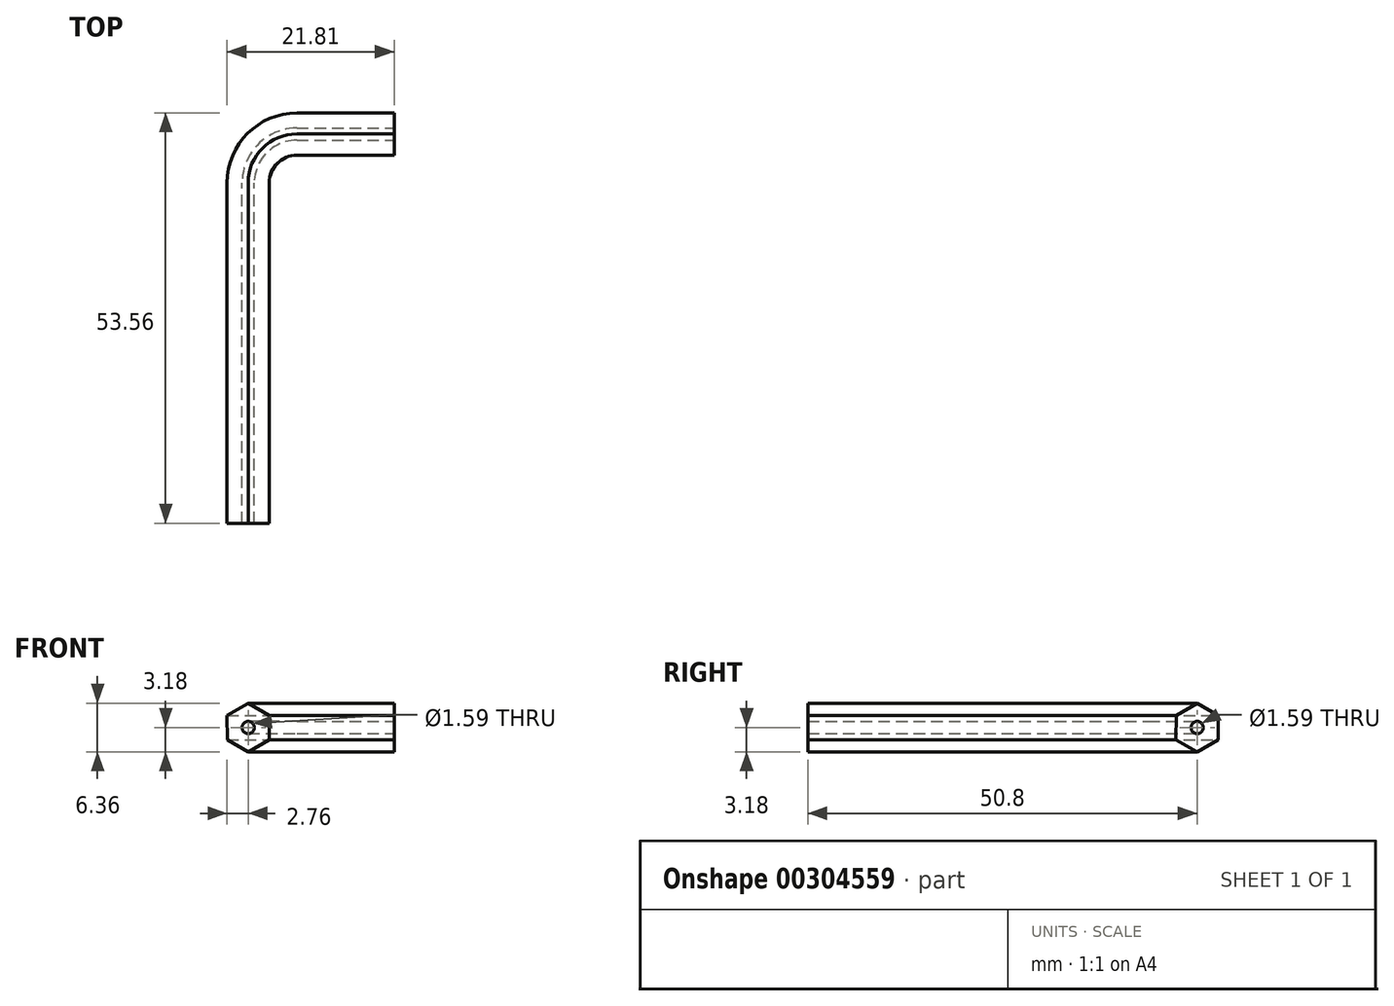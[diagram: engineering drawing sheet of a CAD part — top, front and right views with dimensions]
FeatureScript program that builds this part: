
annotation { "Feature Type Name" : "Feature", "Feature Type Description" : "" }
export const myFeature = defineFeature(function(context is Context, id is Id, definition is map)
    precondition{}
    {
        {
            var Q0;
            Q0=qCreatedBy(makeId("Front.planeOp"),FACE);
            var sketch = newSketch(context, id + "F0", { "sketchPlane" : qUnion([Q0])});
            skCircle(sketch, "E0.cCircle", {"center": v(0, 0) * mm, "radius": 3.18 * mm, "construction": true});
            skLineSegment(sketch, "E0.0", {"start": v(2.76, -1.58) * mm, "end": v(0.01, -3.17) * mm});
            skLineSegment(sketch, "E0.1", {"start": v(0.01, -3.18) * mm, "end": v(-2.74, -1.6) * mm});
            skLineSegment(sketch, "E0.2", {"start": v(-2.74, -1.6) * mm, "end": v(-2.76, 1.58) * mm});
            skLineSegment(sketch, "E0.3", {"start": v(-2.76, 1.58) * mm, "end": v(-0.01, 3.18) * mm});
            skLineSegment(sketch, "E0.4", {"start": v(-0.01, 3.18) * mm, "end": v(2.74, 1.6) * mm});
            skLineSegment(sketch, "E0.5", {"start": v(2.74, 1.6) * mm, "end": v(2.76, -1.58) * mm});
            skSolve(sketch);
        }
        {
            var Q0;
            Q0=qCreatedBy(makeId("Top.planeOp"),FACE);
            var sketch = newSketch(context, id + "F1", { "sketchPlane" : qUnion([Q0])});
            skLineSegment(sketch, "E1", {"start": v(0, 0) * mm, "end": v(0, 44.45) * mm});
            skLineSegment(sketch, "E2", {"start": v(6.35, 50.8) * mm, "end": v(19.05, 50.8) * mm});
            skPoint(sketch, "E3.visualSharp", {"position": v(0, 50.8) * mm});
            skArc(sketch, "E3.filletArc", {"start": v(6.35, 50.8) * mm, "mid": v(1.86, 48.94) * mm, "end": v(0, 44.45) * mm});
            skSolve(sketch);
        }
        {
            var Q0;
            Q0=makeQuery(id+"F0.imprint","IMPRINT",FACE,{"disambiguationData":[TD([[makeQuery(id+"F0.imprint","IMPRINT",EDGE,{"derivedFrom":sQuery(id+"F0.wireOp",EDGE,"E0.0")}),-1.0]])]});
            var Q1;
            Q1 = qConstructionFilter(qBodyType(qCreatedBy(id + "F1" ,EDGE), BodyType.WIRE), ConstructionObject.NO);
            sweep(context, id + "F2", {"profiles" : qUnion([Q0]), "path" : qUnion([Q1])});
        }
        {
            var Q0;
            Q0=qCreatedBy(makeId("Front.planeOp"),FACE);
            var sketch = newSketch(context, id + "F3", { "sketchPlane" : qUnion([Q0])});
            skCircle(sketch, "E4", {"center": v(0, 0) * mm, "radius": 0.8 * mm});
            skSolve(sketch);
        }
        {
            var Q0;
            Q0=makeQuery(id+"F3.imprint","IMPRINT",FACE,{"disambiguationData":[TD([[makeQuery(id+"F3.imprint","IMPRINT",EDGE,{"derivedFrom":sQuery(id+"F3.wireOp",EDGE,"E4")}),1.0]])]});
            var Q1;
            Q1 = qConstructionFilter(qBodyType(qCreatedBy(id + "F1" ,EDGE), BodyType.WIRE), ConstructionObject.NO);
            sweep(context, id + "F4", {"operationType" : NewBodyOperationType.REMOVE, "profiles" : qUnion([Q0]), "path" : qUnion([Q1])});
        }
    });
